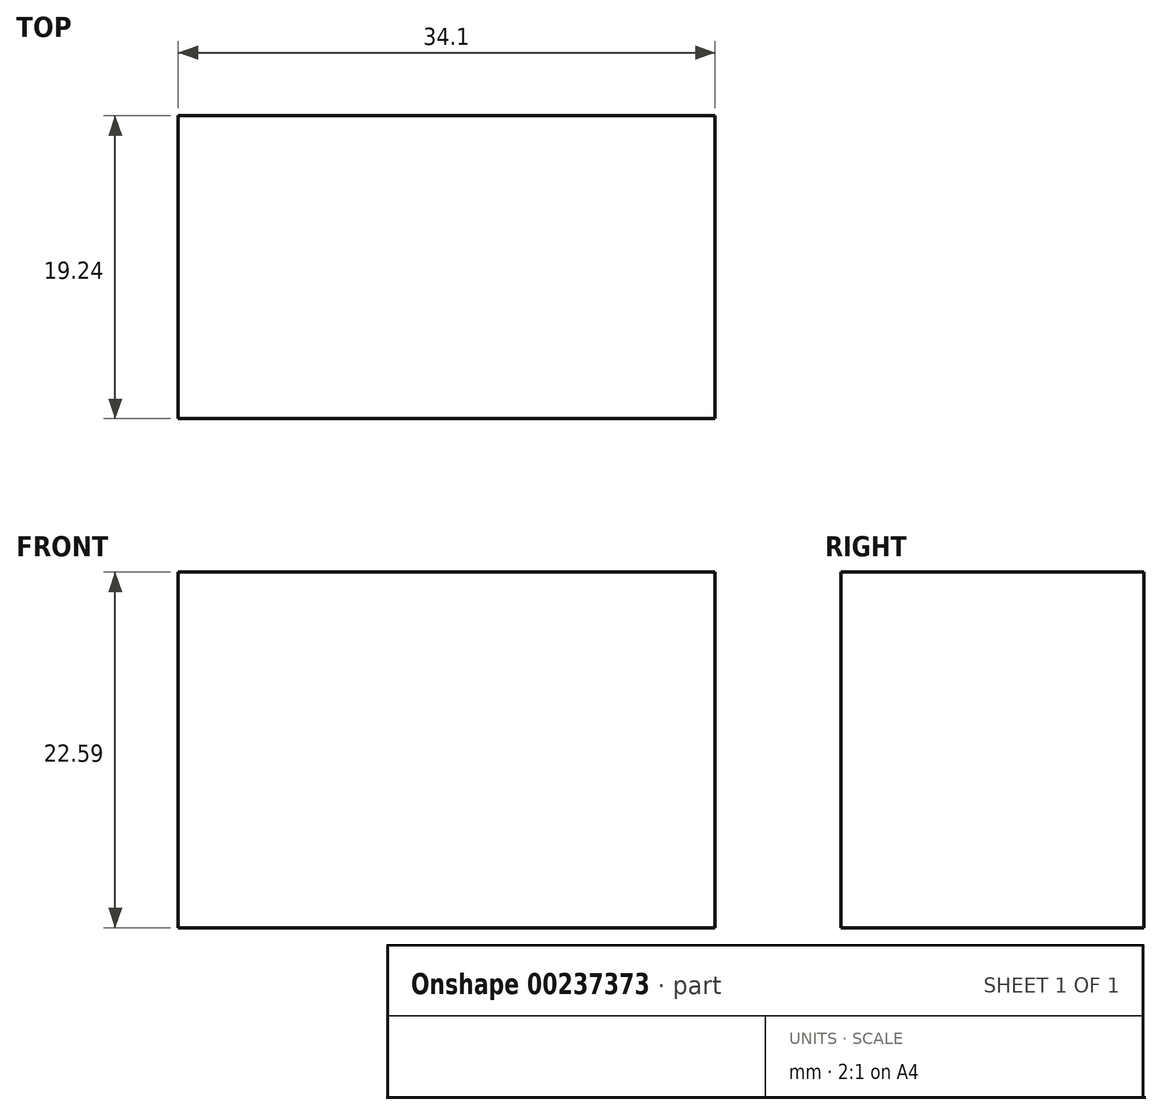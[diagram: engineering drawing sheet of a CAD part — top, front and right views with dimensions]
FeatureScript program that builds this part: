
annotation { "Feature Type Name" : "Feature", "Feature Type Description" : "" }
export const myFeature = defineFeature(function(context is Context, id is Id, definition is map)
    precondition{}
    {
        {
            var Q0;
            Q0=qCreatedBy(makeId("Top.planeOp"),FACE);
            var sketch = newSketch(context, id + "F0", { "sketchPlane" : qUnion([Q0])});
            skLineSegment(sketch, "E0.bottom", {"start": v(0, -2.19) * mm, "end": v(34.1, -2.19) * mm});
            skLineSegment(sketch, "E0.top", {"start": v(0, 17.05) * mm, "end": v(34.1, 17.05) * mm});
            skLineSegment(sketch, "E0.left", {"start": v(0, -2.19) * mm, "end": v(0, 17.05) * mm});
            skLineSegment(sketch, "E0.right", {"start": v(34.1, -2.19) * mm, "end": v(34.1, 17.05) * mm});
            skLineSegment(sketch, "E1", {"start": v(0, -2.19) * mm, "end": v(33.81, -78.53) * mm});
            skSolve(sketch);
        }
        {
            var Q0;
            Q0=qCreatedBy(makeId("Front.planeOp"),FACE);
            var sketch = newSketch(context, id + "F1", { "sketchPlane" : qUnion([Q0])});
            skLineSegment(sketch, "E2", {"start": v(0, 0) * mm, "end": v(0, 22.59) * mm});
            skSolve(sketch);
        }
        {
            var Q0;
            Q0=makeQuery(id+"F0.imprint","IMPRINT",FACE,{"disambiguationData":[TD([[makeQuery(id+"F0.imprint","IMPRINT",EDGE,{"derivedFrom":sQuery(id+"F0.wireOp",EDGE,"E0.bottom")}),1.0]])]});
            var Q1;
            Q1=sQuery(id+"F1.wireOp",EDGE,"E2");
            sweep(context, id + "F2", {"profiles" : qUnion([Q0]), "path" : qUnion([Q1])});
        }
    });
